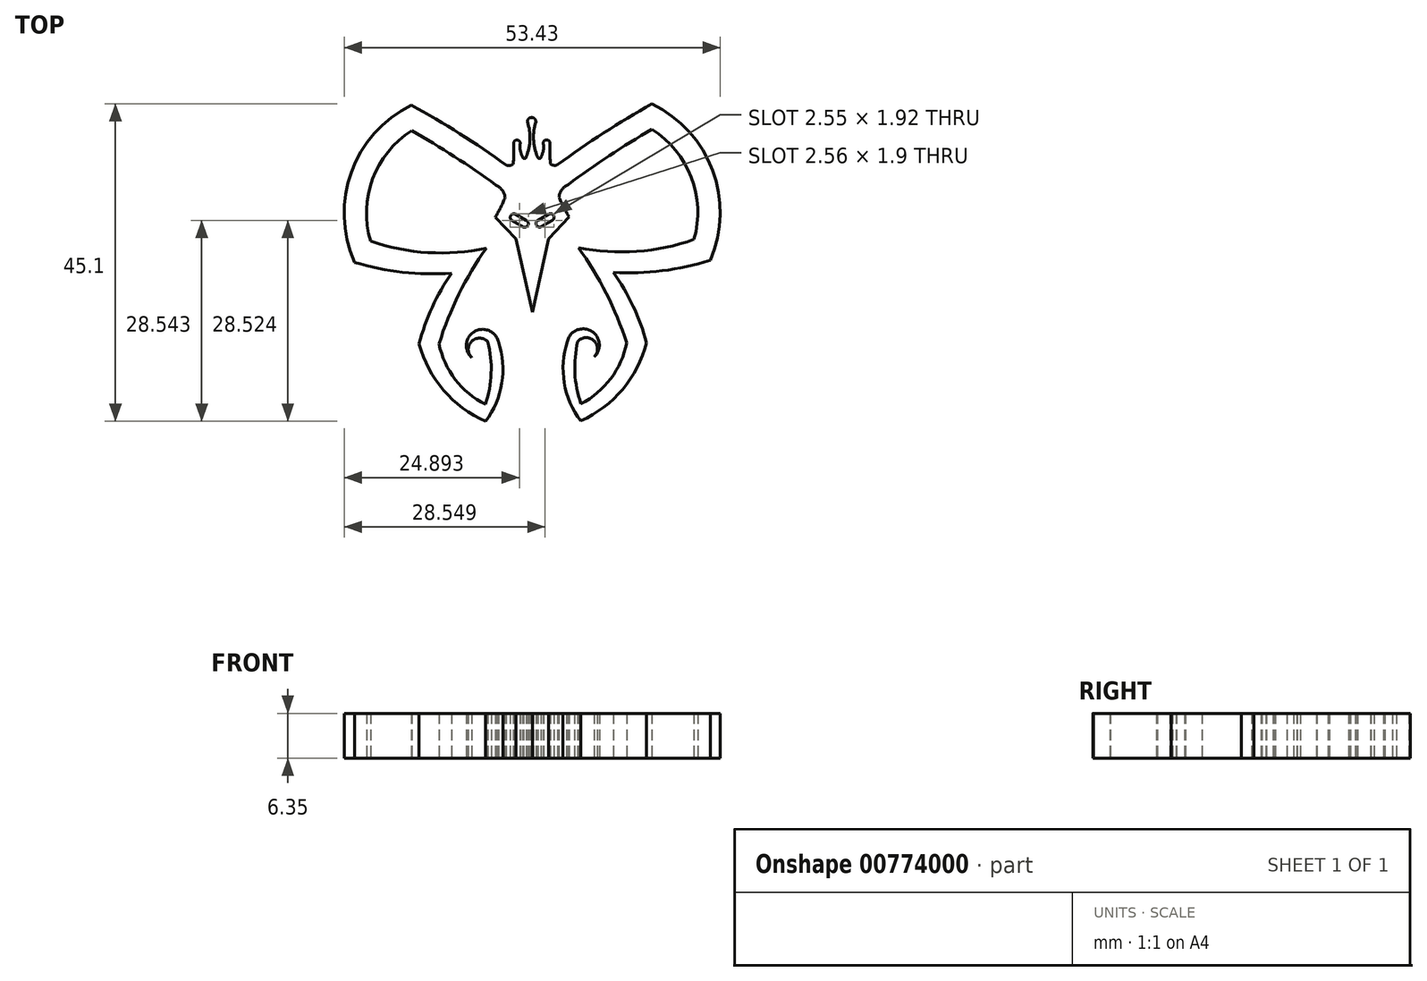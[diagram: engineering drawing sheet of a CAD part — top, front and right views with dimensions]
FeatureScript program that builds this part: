
annotation { "Feature Type Name" : "Feature", "Feature Type Description" : "" }
export const myFeature = defineFeature(function(context is Context, id is Id, definition is map)
    precondition{}
    {
        {
            var Q0;
            Q0=qCreatedBy(makeId("Top.planeOp"),FACE);
            var sketch = newSketch(context, id + "F0", { "sketchPlane" : qUnion([Q0])});
            skLineSegment(sketch, "E0", {"start": v(-0.15, 1.08) * mm, "end": v(0, -26.59) * mm});
            skLineSegment(sketch, "E1", {"start": v(0, -26.59) * mm, "end": v(2.3, -16.14) * mm});
            skPoint(sketch, "E1.endSnap0", {"position": v(-0.07, -13.06) * mm});
            skLineSegment(sketch, "E2", {"start": v(2.3, -16.14) * mm, "end": v(5.17, -13.06) * mm});
            skPoint(sketch, "E3.end.orphan", {"position": v(5.17, -11.52) * mm});
            skPoint(sketch, "E4.orphan", {"position": v(2.97, -13.06) * mm});
            skArc(sketch, "E5", {"start": v(0.45, 0.48) * mm, "mid": v(0.28, 0.9) * mm, "end": v(-0.15, 1.08) * mm});
            skPoint(sketch, "E6.center.orphan", {"position": v(1.32, -5.24) * mm});
            skArc(sketch, "E7", {"start": v(2.45, -2.63) * mm, "mid": v(2, -2.1) * mm, "end": v(1.5, -2.58) * mm});
            skArc(sketch, "E8", {"start": v(2.46, -2.58) * mm, "mid": v(2.44, -4.05) * mm, "end": v(2.54, -5.51) * mm});
            skLineSegment(sketch, "E9.0", {"start": v(4.65, -8.71) * mm, "end": v(5.04, -8.46) * mm});
            skArc(sketch, "E10", {"start": v(2.54, -5.51) * mm, "mid": v(3.02, -5.73) * mm, "end": v(3.54, -5.66) * mm});
            skArc(sketch, "E11", {"start": v(4.79, -8.62) * mm, "mid": v(4.07, -9.31) * mm, "end": v(3.74, -10.26) * mm});
            skArc(sketch, "E12.trimOffspring", {"start": v(3.74, -10.26) * mm, "mid": v(4.4, -11.69) * mm, "end": v(5.17, -13.06) * mm});
            skArc(sketch, "E13", {"start": v(16.92, 3) * mm, "mid": v(10.1, -1.12) * mm, "end": v(3.54, -5.66) * mm});
            skArc(sketch, "E14.0", {"start": v(16.93, -0.62) * mm, "mid": v(10.88, -4.37) * mm, "end": v(5.04, -8.46) * mm});
            skArc(sketch, "E15", {"start": v(25.22, -19.23) * mm, "mid": v(25.56, -6.44) * mm, "end": v(16.92, 3) * mm});
            skArc(sketch, "E16.0", {"start": v(22.93, -16.25) * mm, "mid": v(22.54, -7.43) * mm, "end": v(16.93, -0.62) * mm});
            skArc(sketch, "E17", {"start": v(0.69, -4.5) * mm, "mid": v(0.94, -4.76) * mm, "end": v(1.2, -4.5) * mm});
            skArc(sketch, "E18", {"start": v(0.45, 0.48) * mm, "mid": v(0.13, -2.03) * mm, "end": v(0.69, -4.5) * mm});
            skArc(sketch, "E19", {"start": v(1.2, -4.5) * mm, "mid": v(1.52, -3.57) * mm, "end": v(1.5, -2.58) * mm});
            skPoint(sketch, "E20.center.orphan", {"position": v(0.94, -5.24) * mm});
            skPoint(sketch, "E20.end.orphan", {"position": v(1.25, -5.24) * mm});
            skPoint(sketch, "E21.end.orphan", {"position": v(0.63, -5.24) * mm});
            skArc(sketch, "E22", {"start": v(6.49, -17.4) * mm, "mid": v(14.79, -17.96) * mm, "end": v(22.93, -16.25) * mm});
            skArc(sketch, "E23", {"start": v(11.45, -20.93) * mm, "mid": v(18.41, -20.7) * mm, "end": v(25.22, -19.23) * mm});
            skPoint(sketch, "E24.orphan", {"position": v(26.3, -18.88) * mm});
            skPoint(sketch, "E25.start.orphan", {"position": v(26.3, -15.81) * mm});
            skArc(sketch, "E26", {"start": v(6.85, -42.02) * mm, "mid": v(12.77, -37.54) * mm, "end": v(16.18, -30.94) * mm});
            skArc(sketch, "E27", {"start": v(4.92, -30.74) * mm, "mid": v(4.5, -36.62) * mm, "end": v(6.85, -42.02) * mm});
            skArc(sketch, "E28", {"start": v(13.35, -30.94) * mm, "mid": v(10.44, -23.9) * mm, "end": v(6.49, -17.4) * mm});
            skPoint(sketch, "E29.orphan", {"position": v(6.85, -17.93) * mm});
            skArc(sketch, "E30", {"start": v(16.18, -30.94) * mm, "mid": v(14.26, -25.73) * mm, "end": v(11.45, -20.93) * mm});
            skArc(sketch, "E31", {"start": v(6.85, -39.6) * mm, "mid": v(11.1, -36.02) * mm, "end": v(13.35, -30.94) * mm});
            skArc(sketch, "E32", {"start": v(6.4, -30.74) * mm, "mid": v(6, -35.2) * mm, "end": v(6.85, -39.6) * mm});
            skArc(sketch, "E33", {"start": v(8.74, -32.94) * mm, "mid": v(8.32, -29.26) * mm, "end": v(4.92, -30.74) * mm});
            skArc(sketch, "E34", {"start": v(8.74, -32.94) * mm, "mid": v(8.7, -30.64) * mm, "end": v(6.4, -30.74) * mm});
            skPoint(sketch, "E35.start.orphan", {"position": v(10.04, -17.93) * mm});
            skArc(sketch, "E36", {"start": v(0.75, -13.54) * mm, "mid": v(0.53, -14.2) * mm, "end": v(1.17, -14.48) * mm});
            skArc(sketch, "E37", {"start": v(2.78, -13.55) * mm, "mid": v(2.97, -12.84) * mm, "end": v(2.26, -12.65) * mm});
            skLineSegment(sketch, "E38", {"start": v(0.75, -13.54) * mm, "end": v(2.26, -12.65) * mm});
            skLineSegment(sketch, "E39", {"start": v(1.17, -14.48) * mm, "end": v(2.78, -13.55) * mm});
            skArc(sketch, "E40.MirrorCS", {"start": v(-13.3, -31.08) * mm, "mid": v(-10.47, -24.02) * mm, "end": v(-6.58, -17.48) * mm});
            skPoint(sketch, "E41.MirrorP", {"position": v(-10.13, -18.03) * mm});
            skArc(sketch, "E42.MirrorCS", {"start": v(-6.58, -17.48) * mm, "mid": v(-14.88, -18.12) * mm, "end": v(-23.03, -16.5) * mm});
            skLineSegment(sketch, "E43.MirrorCS", {"start": v(-2.4, -16.16) * mm, "end": v(-5.32, -13.11) * mm});
            skLineSegment(sketch, "E44.MirrorCS", {"start": v(0, -26.59) * mm, "end": v(-2.4, -16.16) * mm});
            skArc(sketch, "E45.MirrorCS", {"start": v(-3.92, -10.3) * mm, "mid": v(-4.55, -11.74) * mm, "end": v(-5.32, -13.11) * mm});
            skArc(sketch, "E46.MirrorCS", {"start": v(-4.98, -8.67) * mm, "mid": v(-4.25, -9.36) * mm, "end": v(-3.92, -10.3) * mm});
            skLineSegment(sketch, "E47.MirrorCS", {"start": v(-4.84, -8.76) * mm, "end": v(-5.23, -8.52) * mm});
            skArc(sketch, "E48.MirrorCS", {"start": v(-8.67, -33.03) * mm, "mid": v(-8.66, -30.73) * mm, "end": v(-6.36, -30.81) * mm});
            skPoint(sketch, "E49.MirrorP", {"position": v(-26.41, -16.1) * mm});
            skArc(sketch, "E50.MirrorCS", {"start": v(-6.36, -30.81) * mm, "mid": v(-5.9, -35.26) * mm, "end": v(-6.72, -39.67) * mm});
            skArc(sketch, "E51.MirrorCS", {"start": v(-8.67, -33.03) * mm, "mid": v(-8.29, -29.35) * mm, "end": v(-4.88, -30.8) * mm});
            skArc(sketch, "E52.MirrorCS", {"start": v(-11.51, -21.05) * mm, "mid": v(-18.48, -20.9) * mm, "end": v(-25.3, -19.5) * mm});
            skArc(sketch, "E53.MirrorCS", {"start": v(-25.3, -19.5) * mm, "mid": v(-25.77, -6.71) * mm, "end": v(-17.23, 2.83) * mm});
            skPoint(sketch, "E54.MirrorP", {"position": v(-5.33, -11.57) * mm});
            skPoint(sketch, "E55.MirrorP", {"position": v(-26.38, -19.16) * mm});
            skArc(sketch, "E56.MirrorCS", {"start": v(-16.14, -31.11) * mm, "mid": v(-14.27, -25.88) * mm, "end": v(-11.51, -21.05) * mm});
            skArc(sketch, "E57.MirrorCS", {"start": v(-4.88, -30.8) * mm, "mid": v(-4.39, -36.67) * mm, "end": v(-6.7, -42.1) * mm});
            skPoint(sketch, "E58.MirrorP", {"position": v(-3.1, -13.09) * mm});
            skPoint(sketch, "E59.MirrorP", {"position": v(-6.95, -18) * mm});
            skArc(sketch, "E60.MirrorCS", {"start": v(-17.23, 2.83) * mm, "mid": v(-10.37, -1.23) * mm, "end": v(-3.76, -5.7) * mm});
            skArc(sketch, "E61.MirrorCS", {"start": v(-23.03, -16.5) * mm, "mid": v(-22.74, -7.67) * mm, "end": v(-17.2, -0.8) * mm});
            skArc(sketch, "E62.MirrorCS", {"start": v(-17.2, -0.8) * mm, "mid": v(-11.11, -4.5) * mm, "end": v(-5.23, -8.52) * mm});
            skArc(sketch, "E63.MirrorCS", {"start": v(-6.7, -42.1) * mm, "mid": v(-12.66, -37.67) * mm, "end": v(-16.14, -31.11) * mm});
            skArc(sketch, "E64.MirrorCS", {"start": v(-6.72, -39.67) * mm, "mid": v(-11, -36.14) * mm, "end": v(-13.3, -31.08) * mm});
            skArc(sketch, "E65.MirrorCS", {"start": v(-0.92, -4.51) * mm, "mid": v(-1.17, -4.77) * mm, "end": v(-1.43, -4.52) * mm});
            skArc(sketch, "E66.MirrorCS", {"start": v(-2.76, -5.54) * mm, "mid": v(-3.24, -5.77) * mm, "end": v(-3.76, -5.7) * mm});
            skArc(sketch, "E67.MirrorCS", {"start": v(-0.89, -13.54) * mm, "mid": v(-0.66, -14.2) * mm, "end": v(-1.3, -14.5) * mm});
            skArc(sketch, "E68.MirrorCS", {"start": v(-2.92, -13.58) * mm, "mid": v(-3.12, -12.87) * mm, "end": v(-2.4, -12.68) * mm});
            skLineSegment(sketch, "E69.MirrorCS", {"start": v(-1.3, -14.5) * mm, "end": v(-2.92, -13.58) * mm});
            skLineSegment(sketch, "E70.MirrorCS", {"start": v(-0.89, -13.54) * mm, "end": v(-2.4, -12.68) * mm});
            skArc(sketch, "E71.MirrorCS", {"start": v(-1.43, -4.52) * mm, "mid": v(-1.76, -3.59) * mm, "end": v(-1.75, -2.6) * mm});
            skArc(sketch, "E72.MirrorCS", {"start": v(-0.74, 0.47) * mm, "mid": v(-0.39, -2.03) * mm, "end": v(-0.92, -4.51) * mm});
            skArc(sketch, "E73.MirrorCS", {"start": v(-2.7, -2.6) * mm, "mid": v(-2.68, -4.08) * mm, "end": v(-2.76, -5.54) * mm});
            skArc(sketch, "E74.MirrorCS", {"start": v(-2.7, -2.66) * mm, "mid": v(-2.26, -2.13) * mm, "end": v(-1.75, -2.6) * mm});
            skPoint(sketch, "E75.MirrorP", {"position": v(-1.17, -5.25) * mm});
            skArc(sketch, "E76.MirrorCS", {"start": v(-0.74, 0.47) * mm, "mid": v(-0.57, 0.9) * mm, "end": v(-0.15, 1.08) * mm});
            skPoint(sketch, "E77.MirrorP", {"position": v(-1.48, -5.25) * mm});
            skPoint(sketch, "E78.MirrorP", {"position": v(-1.54, -5.25) * mm});
            skPoint(sketch, "E79.MirrorP", {"position": v(-0.86, -5.25) * mm});
            skSolve(sketch);
        }
        {
            var Q0;
            Q0=makeQuery(id+"F0.imprint","IMPRINT",FACE,{"disambiguationData":[TD([[makeQuery(id+"F0.imprint","IMPRINT",EDGE,{"derivedFrom":sQuery(id+"F0.wireOp",EDGE,"E0")}),1.0]])]});
            var Q1;
            Q1=makeQuery(id+"F0.imprint","IMPRINT",FACE,{"disambiguationData":[TD([[makeQuery(id+"F0.imprint","IMPRINT",EDGE,{"derivedFrom":sQuery(id+"F0.wireOp",EDGE,"E0")}),-1.0]])]});
            extrude(context, id + "F1", {"entities" : qUnion([Q0, Q1]), "depth" : 6.35 * mm, "offsetDistance" : 25.4 * mm});
        }
    });
